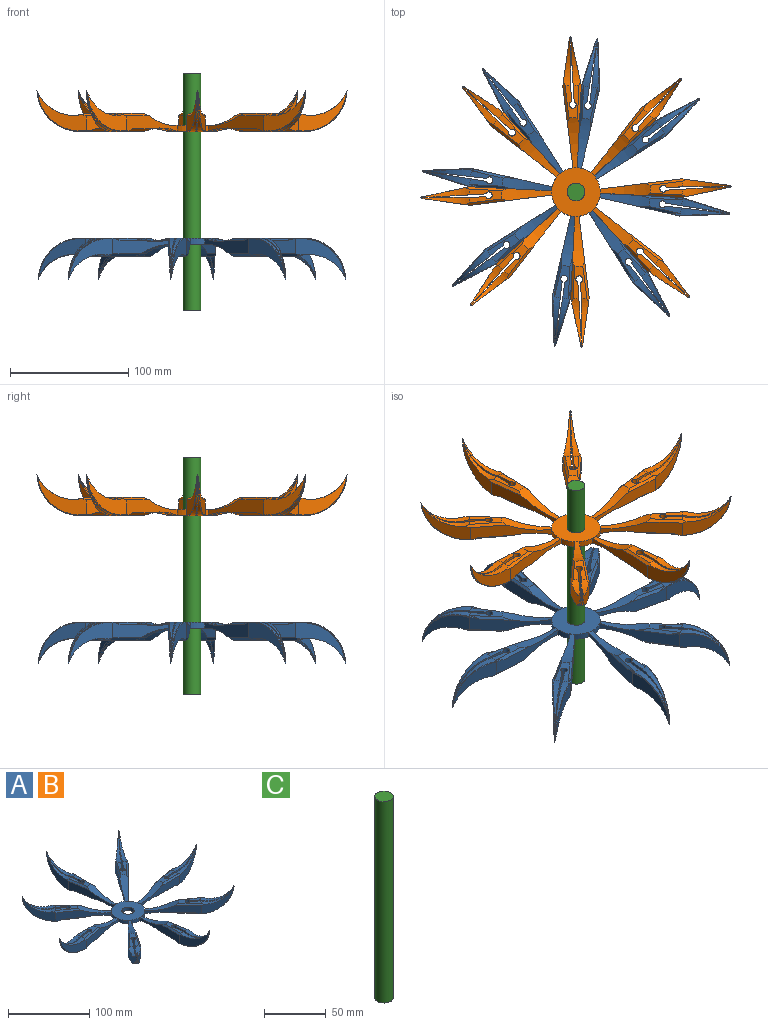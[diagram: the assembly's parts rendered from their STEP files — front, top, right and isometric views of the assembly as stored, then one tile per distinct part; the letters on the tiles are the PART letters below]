
ASSEMBLY  parts=3 mates=2
PART A: 179 faces, bbox 267x267x47 mm
  f0: cylinder r=20.6mm len=10.99mm, axis (0,0,-1), area 63.2mm2, adj f12,f14,f49,f155
  f1: cylinder r=20.6mm len=11.81mm, axis (0,0,-1), area 63.2mm2, adj f12,f14,f112,f178
  f2: cylinder r=20.6mm len=10.99mm, axis (0,0,-1), area 63.2mm2, adj f12,f14,f74,f177
  f3: cylinder r=20.6mm len=11.81mm, axis (0,0,-1), area 63.2mm2, adj f12,f14,f134,f154
  f4: cylinder r=20.6mm len=10.99mm, axis (0,0,-1), area 63.2mm2, adj f12,f14,f113,f133
  f5: cylinder r=20.6mm len=10.99mm, axis (0,0,-1), area 63.2mm2, adj f9,f12,f14,f71
  f6: cylinder r=20.6mm len=11.81mm, axis (0,0,-1), area 63.2mm2, adj f12,f14,f50,f70
  f7: torus R=100.19mm, axis (0,0,-1), area 159.5mm2, adj f8,f16,f21,f24,f28,f30
  f8: torus R=94.49mm, axis (0,0,-1), area 157mm2, adj f7,f9,f17,f24,f26,f30
  f9: plane 68.36x13.03mm, normal (0.17,-0.98,0), area 553.1mm2, adj f5,f8,f15,f18,f21,f26,f28,f30
  f10: torus R=100.19mm, axis (0,0,-1), area 159.5mm2, adj f11,f16,f20,f23,f27,f29
  f11: torus R=94.49mm, axis (0,0,-1), area 157mm2, adj f10,f17,f19,f23,f25,f29
  f12: plane 41.19x41.19mm, normal (0,0,1), area 1156mm2, adj f0,f1,f2,f3,f4,f5,f6,f13
  f13: cylinder r=20.6mm len=11.81mm, axis (0,0,-1), area 63.2mm2, adj f12,f14,f19,f75
  f14: plane 41.19x41.19mm, normal (0,0,-1), area 1156mm2, adj f0,f1,f2,f3,f4,f5,f6,f13
  f15: torus R=23.9mm, axis (0,0,-1), area 314.2mm2, adj f9,f12,f16,f19,f27,f28
  f16: plane 27.86x11.66mm, normal (0,0,1), area 198.1mm2, adj f7,f10,f15,f22,f23,f24,f27,f28
  f17: plane 27.86x11.66mm, normal (0,0,-1), area 198.1mm2, adj f8,f11,f18,f22,f23,f24,f25,f26
  f18: torus R=41.68mm, axis (0,0,-1), area 291.7mm2, adj f9,f14,f17,f19,f25,f26
  f19: plane 69.41x13.03mm, normal (0,1,0), area 553.1mm2, adj f11,f13,f15,f18,f20,f25,f27,f29
  f20: plane 40.14x33.27mm, normal (-0.26,0.97,0), area 440.2mm2, adj f10,f19,f27,f29
  f21: plane 41.4x33.27mm, normal (-0.09,-1,0), area 440.2mm2, adj f7,f9,f28,f30
  f22: cylinder r=2.87mm len=15.02mm, axis (0,0,1), area 231.7mm2, adj f16,f17,f23,f24
  f23: plane 54.41x34.53mm, normal (0.11,-0.99,0), area 665.3mm2, adj f10,f11,f16,f17,f22
  f24: plane 54.62x34.53mm, normal (-0.07,1,0), area 665.4mm2, adj f7,f8,f16,f17,f22
  f25: plane 36.97x2.14mm, normal (0,0.71,-0.71), area 75.7mm2, adj f11,f17,f18,f19
  f26: plane 36.75x5.42mm, normal (0.12,-0.7,-0.71), area 75.7mm2, adj f8,f9,f17,f18
  f27: plane 34.89x2.01mm, normal (0,0.71,0.71), area 87.5mm2, adj f10,f15,f16,f19,f20
  f28: plane 34.54x6.72mm, normal (0.12,-0.7,0.71), area 87.5mm2, adj f7,f9,f15,f16,f21
  f29: bspline ~42.44x34.55mm, area 39.4mm2, adj f10,f11,f19,f20
  f30: bspline ~43.75x34.55mm, area 39.4mm2, adj f7,f8,f9,f21
  f31: cylinder r=7.5mm len=15mm, axis (0,0,-1), area 236.7mm2, adj f12,f14
  f32: cylinder r=2.87mm len=15.02mm, axis (0,0,1), area 231.7mm2, adj f33,f35,f37,f38
  f33: plane 54.62x34.53mm, normal (-1,-0.07,0), area 665.4mm2, adj f32,f34,f37,f38,f41
  f34: torus R=100.19mm, axis (0,0,-1), area 159.5mm2, adj f33,f37,f39,f41,f42,f43
  f35: plane 54.41x34.53mm, normal (0.99,0.11,0), area 665.3mm2, adj f32,f36,f37,f38,f48
  f36: torus R=100.19mm, axis (0,0,-1), area 159.5mm2, adj f35,f37,f45,f46,f47,f48
  f37: plane 27.86x11.66mm, normal (0,0,1), area 198.1mm2, adj f32,f33,f34,f35,f36,f39,f45,f52
  f38: plane 27.86x11.66mm, normal (0,0,-1), area 198.1mm2, adj f32,f33,f35,f40,f41,f44,f48,f51
  f39: plane 34.54x6.72mm, normal (0.7,0.12,0.71), area 87.5mm2, adj f34,f37,f43,f49,f52
  f40: plane 36.75x5.42mm, normal (0.7,0.12,-0.71), area 75.7mm2, adj f38,f41,f49,f51
  f41: torus R=94.49mm, axis (0,0,-1), area 157mm2, adj f33,f34,f38,f40,f42,f49
  f42: bspline ~43.75x34.55mm, area 39.4mm2, adj f34,f41,f43,f49
  f43: plane 41.4x33.27mm, normal (1,-0.09,0), area 440.2mm2, adj f34,f39,f42,f49
  f44: plane 36.97x2.14mm, normal (-0.71,0,-0.71), area 75.7mm2, adj f38,f48,f50,f51
  f45: plane 34.89x2.01mm, normal (-0.71,0,0.71), area 87.5mm2, adj f36,f37,f46,f50,f52
  f46: plane 40.14x33.27mm, normal (-0.97,-0.26,0), area 440.2mm2, adj f36,f45,f47,f50
  f47: bspline ~42.44x34.55mm, area 39.4mm2, adj f36,f46,f48,f50
  f48: torus R=94.49mm, axis (0,0,-1), area 157mm2, adj f35,f36,f38,f44,f47,f50
  f49: plane 68.36x13.03mm, normal (0.98,0.17,0), area 553.1mm2, adj f0,f39,f40,f41,f42,f43,f51,f52
  f50: plane 69.41x13.03mm, normal (-1,0,0), area 553.1mm2, adj f6,f44,f45,f46,f47,f48,f51,f52
  f51: torus R=41.68mm, axis (0,0,-1), area 291.7mm2, adj f14,f38,f40,f44,f49,f50
  f52: torus R=23.9mm, axis (0,0,-1), area 314.2mm2, adj f12,f37,f39,f45,f49,f50
  f53: cylinder r=2.87mm len=15.02mm, axis (0,0,1), area 231.7mm2, adj f54,f56,f58,f59
  f54: plane 42.69x34.53mm, normal (0.78,-0.63,0), area 665.3mm2, adj f53,f55,f58,f59,f64
  f55: torus R=100.19mm, axis (0,0,-1), area 159.5mm2, adj f54,f58,f61,f62,f63,f64
  f56: plane 41.15x36.09mm, normal (-0.75,0.66,0), area 665.4mm2, adj f53,f57,f58,f59,f67
  f57: torus R=100.19mm, axis (0,0,-1), area 159.5mm2, adj f56,f58,f65,f67,f68,f69
  f58: plane 26.79x24.59mm, normal (0,0,1), area 198.1mm2, adj f53,f54,f55,f56,f57,f61,f65,f73
  f59: plane 26.79x24.59mm, normal (0,0,-1), area 198.1mm2, adj f53,f54,f56,f60,f64,f66,f67,f72
  f60: plane 27.59x24.77mm, normal (-0.5,0.5,-0.71), area 75.7mm2, adj f59,f64,f71,f72
  f61: plane 25.4x23.96mm, normal (-0.5,0.5,0.71), area 87.5mm2, adj f55,f58,f62,f71,f73
  f62: plane 36x33.27mm, normal (-0.87,0.5,0), area 440.2mm2, adj f55,f61,f63,f71
  f63: bspline ~38.16x34.55mm, area 39.4mm2, adj f55,f62,f64,f71
  f64: torus R=94.49mm, axis (0,0,-1), area 157mm2, adj f54,f55,f59,f60,f63,f71
  f65: plane 28x20.85mm, normal (0.58,-0.41,0.71), area 87.5mm2, adj f57,f58,f69,f70,f73
  f66: plane 29.16x22.9mm, normal (0.58,-0.41,-0.71), area 75.7mm2, adj f59,f67,f70,f72
  f67: torus R=94.49mm, axis (0,0,-1), area 157mm2, adj f56,f57,f59,f66,f68,f70
  f68: bspline ~34.55x33.83mm, area 39.4mm2, adj f57,f67,f69,f70
  f69: plane 33.27x31.86mm, normal (0.64,-0.77,0), area 440.2mm2, adj f57,f65,f68,f70
  f70: plane 56.86x39.81mm, normal (0.82,-0.57,0), area 553.1mm2, adj f6,f65,f66,f67,f68,f69,f72,f73
  f71: plane 49.08x49.08mm, normal (-0.71,0.71,0), area 553.1mm2, adj f5,f60,f61,f62,f63,f64,f72,f73
  f72: torus R=41.68mm, axis (0,0,-1), area 291.7mm2, adj f14,f59,f60,f66,f70,f71
  f73: torus R=23.9mm, axis (0,0,-1), area 314.2mm2, adj f12,f58,f61,f65,f70,f71
  f74: plane 49.08x49.08mm, normal (0.71,0.71,0), area 553.1mm2, adj f2,f76,f77,f79,f81,f87,f88,f89
  f75: plane 56.86x39.81mm, normal (-0.57,-0.82,0), area 553.1mm2, adj f13,f76,f77,f80,f83,f84,f85,f86
  f76: torus R=41.68mm, axis (0,0,-1), area 291.7mm2, adj f14,f74,f75,f78,f79,f80
  f77: torus R=23.9mm, axis (0,0,-1), area 314.2mm2, adj f12,f74,f75,f81,f82,f83
  f78: plane 26.79x24.59mm, normal (0,0,-1), area 198.1mm2, adj f76,f79,f80,f86,f87,f90,f91,f92
  f79: plane 27.59x24.77mm, normal (0.5,0.5,-0.71), area 75.7mm2, adj f74,f76,f78,f87
  f80: plane 29.16x22.9mm, normal (-0.41,-0.58,-0.71), area 75.7mm2, adj f75,f76,f78,f86
  f81: plane 25.4x23.96mm, normal (0.5,0.5,0.71), area 87.5mm2, adj f74,f77,f82,f89,f93
  f82: plane 26.79x24.59mm, normal (0,0,1), area 198.1mm2, adj f77,f81,f83,f90,f91,f92,f93,f94
  f83: plane 28x20.85mm, normal (-0.41,-0.58,0.71), area 87.5mm2, adj f75,f77,f82,f84,f94
  f84: plane 33.27x31.86mm, normal (-0.77,-0.64,0), area 440.2mm2, adj f75,f83,f85,f94
  f85: bspline ~34.55x33.83mm, area 39.4mm2, adj f75,f84,f86,f94
  f86: torus R=94.49mm, axis (0,0,-1), area 157mm2, adj f75,f78,f80,f85,f90,f94
  f87: torus R=94.49mm, axis (0,0,-1), area 157mm2, adj f74,f78,f79,f88,f92,f93
  f88: bspline ~38.16x34.55mm, area 39.4mm2, adj f74,f87,f89,f93
  f89: plane 36x33.27mm, normal (0.5,0.87,0), area 440.2mm2, adj f74,f81,f88,f93
  f90: plane 41.15x36.09mm, normal (0.66,0.75,0), area 665.4mm2, adj f78,f82,f86,f91,f94
  f91: cylinder r=2.87mm len=15.02mm, axis (0,0,1), area 231.7mm2, adj f78,f82,f90,f92
  f92: plane 42.69x34.53mm, normal (-0.63,-0.78,0), area 665.3mm2, adj f78,f82,f87,f91,f93
  f93: torus R=100.19mm, axis (0,0,-1), area 159.5mm2, adj f81,f82,f87,f88,f89,f92
  f94: torus R=100.19mm, axis (0,0,-1), area 159.5mm2, adj f82,f83,f84,f85,f86,f90
  f95: cylinder r=2.87mm len=15.02mm, axis (0,0,1), area 231.7mm2, adj f96,f98,f100,f101
  f96: plane 41.15x36.09mm, normal (0.75,-0.66,0), area 665.4mm2, adj f95,f97,f100,f101,f104
  f97: torus R=100.19mm, axis (0,0,-1), area 159.5mm2, adj f96,f100,f102,f104,f105,f106
  f98: plane 42.69x34.53mm, normal (-0.78,0.63,0), area 665.3mm2, adj f95,f99,f100,f101,f111
  f99: torus R=100.19mm, axis (0,0,-1), area 159.5mm2, adj f98,f100,f108,f109,f110,f111
  f100: plane 26.79x24.59mm, normal (0,0,1), area 198.1mm2, adj f95,f96,f97,f98,f99,f102,f108,f115
  f101: plane 26.79x24.59mm, normal (0,0,-1), area 198.1mm2, adj f95,f96,f98,f103,f104,f107,f111,f114
  f102: plane 28x20.85mm, normal (-0.58,0.41,0.71), area 87.5mm2, adj f97,f100,f106,f112,f115
  f103: plane 29.16x22.9mm, normal (-0.58,0.41,-0.71), area 75.7mm2, adj f101,f104,f112,f114
  f104: torus R=94.49mm, axis (0,0,-1), area 157mm2, adj f96,f97,f101,f103,f105,f112
  f105: bspline ~34.55x33.83mm, area 39.4mm2, adj f97,f104,f106,f112
  f106: plane 33.27x31.86mm, normal (-0.64,0.77,0), area 440.2mm2, adj f97,f102,f105,f112
  f107: plane 27.59x24.77mm, normal (0.5,-0.5,-0.71), area 75.7mm2, adj f101,f111,f113,f114
  f108: plane 25.4x23.96mm, normal (0.5,-0.5,0.71), area 87.5mm2, adj f99,f100,f109,f113,f115
  f109: plane 36x33.27mm, normal (0.87,-0.5,0), area 440.2mm2, adj f99,f108,f110,f113
  f110: bspline ~38.16x34.55mm, area 39.4mm2, adj f99,f109,f111,f113
  f111: torus R=94.49mm, axis (0,0,-1), area 157mm2, adj f98,f99,f101,f107,f110,f113
  f112: plane 56.86x39.81mm, normal (-0.82,0.57,0), area 553.1mm2, adj f1,f102,f103,f104,f105,f106,f114,f115
  f113: plane 49.08x49.08mm, normal (0.71,-0.71,0), area 553.1mm2, adj f4,f107,f108,f109,f110,f111,f114,f115
  f114: torus R=41.68mm, axis (0,0,-1), area 291.7mm2, adj f14,f101,f103,f107,f112,f113
  f115: torus R=23.9mm, axis (0,0,-1), area 314.2mm2, adj f12,f100,f102,f108,f112,f113
  f116: cylinder r=2.87mm len=15.02mm, axis (0,0,1), area 231.7mm2, adj f117,f119,f121,f122
  f117: plane 54.41x34.53mm, normal (-0.11,0.99,0), area 665.3mm2, adj f116,f118,f121,f122,f127
  f118: torus R=100.19mm, axis (0,0,-1), area 159.5mm2, adj f117,f121,f124,f125,f126,f127
  f119: plane 54.62x34.53mm, normal (0.07,-1,0), area 665.4mm2, adj f116,f120,f121,f122,f130
  f120: torus R=100.19mm, axis (0,0,-1), area 159.5mm2, adj f119,f121,f128,f130,f131,f132
  f121: plane 27.86x11.66mm, normal (0,0,1), area 198.1mm2, adj f116,f117,f118,f119,f120,f124,f128,f136
  f122: plane 27.86x11.66mm, normal (0,0,-1), area 198.1mm2, adj f116,f117,f119,f123,f127,f129,f130,f135
  f123: plane 36.97x2.14mm, normal (0,-0.71,-0.71), area 75.7mm2, adj f122,f127,f134,f135
  f124: plane 34.89x2.01mm, normal (0,-0.71,0.71), area 87.5mm2, adj f118,f121,f125,f134,f136
  f125: plane 40.14x33.27mm, normal (0.26,-0.97,0), area 440.2mm2, adj f118,f124,f126,f134
  f126: bspline ~42.44x34.55mm, area 39.4mm2, adj f118,f125,f127,f134
  f127: torus R=94.49mm, axis (0,0,-1), area 157mm2, adj f117,f118,f122,f123,f126,f134
  f128: plane 34.54x6.72mm, normal (-0.12,0.7,0.71), area 87.5mm2, adj f120,f121,f132,f133,f136
  f129: plane 36.75x5.42mm, normal (-0.12,0.7,-0.71), area 75.7mm2, adj f122,f130,f133,f135
  f130: torus R=94.49mm, axis (0,0,-1), area 157mm2, adj f119,f120,f122,f129,f131,f133
  f131: bspline ~43.75x34.55mm, area 39.4mm2, adj f120,f130,f132,f133
  f132: plane 41.4x33.27mm, normal (0.09,1,0), area 440.2mm2, adj f120,f128,f131,f133
  f133: plane 68.36x13.03mm, normal (-0.17,0.98,0), area 553.1mm2, adj f4,f128,f129,f130,f131,f132,f135,f136
  f134: plane 69.41x13.03mm, normal (0,-1,0), area 553.1mm2, adj f3,f123,f124,f125,f126,f127,f135,f136
  f135: torus R=41.68mm, axis (0,0,-1), area 291.7mm2, adj f14,f122,f123,f129,f133,f134
  f136: torus R=23.9mm, axis (0,0,-1), area 314.2mm2, adj f12,f121,f124,f128,f133,f134
  f137: cylinder r=2.87mm len=15.02mm, axis (0,0,1), area 231.7mm2, adj f138,f140,f142,f143
  f138: plane 42.69x34.53mm, normal (0.63,0.78,0), area 665.3mm2, adj f137,f139,f142,f143,f148
  f139: torus R=100.19mm, axis (0,0,-1), area 159.5mm2, adj f138,f142,f145,f146,f147,f148
  f140: plane 41.15x36.09mm, normal (-0.66,-0.75,0), area 665.4mm2, adj f137,f141,f142,f143,f151
  f141: torus R=100.19mm, axis (0,0,-1), area 159.5mm2, adj f140,f142,f149,f151,f152,f153
  f142: plane 26.79x24.59mm, normal (0,0,1), area 198.1mm2, adj f137,f138,f139,f140,f141,f145,f149,f157
  f143: plane 26.79x24.59mm, normal (0,0,-1), area 198.1mm2, adj f137,f138,f140,f144,f148,f150,f151,f156
  f144: plane 27.59x24.77mm, normal (-0.5,-0.5,-0.71), area 75.7mm2, adj f143,f148,f155,f156
  f145: plane 25.4x23.96mm, normal (-0.5,-0.5,0.71), area 87.5mm2, adj f139,f142,f146,f155,f157
  f146: plane 36x33.27mm, normal (-0.5,-0.87,0), area 440.2mm2, adj f139,f145,f147,f155
  f147: bspline ~38.16x34.55mm, area 39.4mm2, adj f139,f146,f148,f155
  f148: torus R=94.49mm, axis (0,0,-1), area 157mm2, adj f138,f139,f143,f144,f147,f155
  f149: plane 28x20.85mm, normal (0.41,0.58,0.71), area 87.5mm2, adj f141,f142,f153,f154,f157
  f150: plane 29.16x22.9mm, normal (0.41,0.58,-0.71), area 75.7mm2, adj f143,f151,f154,f156
  f151: torus R=94.49mm, axis (0,0,-1), area 157mm2, adj f140,f141,f143,f150,f152,f154
  f152: bspline ~34.55x33.83mm, area 39.4mm2, adj f141,f151,f153,f154
  f153: plane 33.27x31.86mm, normal (0.77,0.64,0), area 440.2mm2, adj f141,f149,f152,f154
  f154: plane 56.86x39.81mm, normal (0.57,0.82,0), area 553.1mm2, adj f3,f149,f150,f151,f152,f153,f156,f157
  f155: plane 49.08x49.08mm, normal (-0.71,-0.71,0), area 553.1mm2, adj f0,f144,f145,f146,f147,f148,f156,f157
  f156: torus R=41.68mm, axis (0,0,-1), area 291.7mm2, adj f14,f143,f144,f150,f154,f155
  f157: torus R=23.9mm, axis (0,0,-1), area 314.2mm2, adj f12,f142,f145,f149,f154,f155
  f158: torus R=100.19mm, axis (0,0,-1), area 159.5mm2, adj f162,f166,f167,f168,f169,f170
  f159: torus R=100.19mm, axis (0,0,-1), area 159.5mm2, adj f160,f163,f164,f165,f170,f171
  f160: plane 54.41x34.53mm, normal (-0.99,-0.11,0), area 665.3mm2, adj f159,f161,f165,f170,f174
  f161: cylinder r=2.87mm len=15.02mm, axis (0,0,1), area 231.7mm2, adj f160,f162,f170,f174
  f162: plane 54.62x34.53mm, normal (1,0.07,0), area 665.4mm2, adj f158,f161,f166,f170,f174
  f163: plane 40.14x33.27mm, normal (0.97,0.26,0), area 440.2mm2, adj f159,f164,f171,f178
  f164: bspline ~42.44x34.55mm, area 39.4mm2, adj f159,f163,f165,f178
  f165: torus R=94.49mm, axis (0,0,-1), area 157mm2, adj f159,f160,f164,f173,f174,f178
  f166: torus R=94.49mm, axis (0,0,-1), area 157mm2, adj f158,f162,f167,f172,f174,f177
  f167: bspline ~43.75x34.55mm, area 39.4mm2, adj f158,f166,f168,f177
  f168: plane 41.4x33.27mm, normal (-1,0.09,0), area 440.2mm2, adj f158,f167,f169,f177
  f169: plane 34.54x6.72mm, normal (-0.7,-0.12,0.71), area 87.5mm2, adj f158,f168,f170,f175,f177
  f170: plane 27.86x11.66mm, normal (0,0,1), area 198.1mm2, adj f158,f159,f160,f161,f162,f169,f171,f175
  f171: plane 34.89x2.01mm, normal (0.71,0,0.71), area 87.5mm2, adj f159,f163,f170,f175,f178
  f172: plane 36.75x5.42mm, normal (-0.7,-0.12,-0.71), area 75.7mm2, adj f166,f174,f176,f177
  f173: plane 36.97x2.14mm, normal (0.71,0,-0.71), area 75.7mm2, adj f165,f174,f176,f178
  f174: plane 27.86x11.66mm, normal (0,0,-1), area 198.1mm2, adj f160,f161,f162,f165,f166,f172,f173,f176
  f175: torus R=23.9mm, axis (0,0,-1), area 314.2mm2, adj f12,f169,f170,f171,f177,f178
  f176: torus R=41.68mm, axis (0,0,-1), area 291.7mm2, adj f14,f172,f173,f174,f177,f178
  f177: plane 68.36x13.03mm, normal (-0.98,-0.17,0), area 553.1mm2, adj f2,f166,f167,f168,f169,f172,f175,f176
  f178: plane 69.41x13.03mm, normal (1,0,0), area 553.1mm2, adj f1,f163,f164,f165,f171,f173,f175,f176
PART B: same geometry as A
PART C: 3 faces, bbox 15x15x200 mm
  f0: cylinder r=7.5mm len=200mm, axis (0,0,-1), area 9424.8mm2, adj f1,f2
  f1: plane 15x15mm, normal (0,0,1), area 176.7mm2, adj f0
  f2: plane 15x15mm, normal (0,0,-1), area 176.7mm2, adj f0
PLACE A rot(axis=(-0.41,-0.91,0),180deg) t=(232.72,-9.44,4.12)mm
PLACE B rot(axis=(0,0,-1),137.9deg) t=(232.72,-9.44,94.59)mm
PLACE C rot(axis=(0,0,-1),47.9deg) t=(232.72,-9.44,43.32)mm
MATE slider B.f0 <-> C.f0  axis (0,0,1) through (232.72,-9.44,99.62)mm
MATE slider A.f0 <-> C.f0  axis (0,0,1) through (232.72,-9.44,4.12)mm
